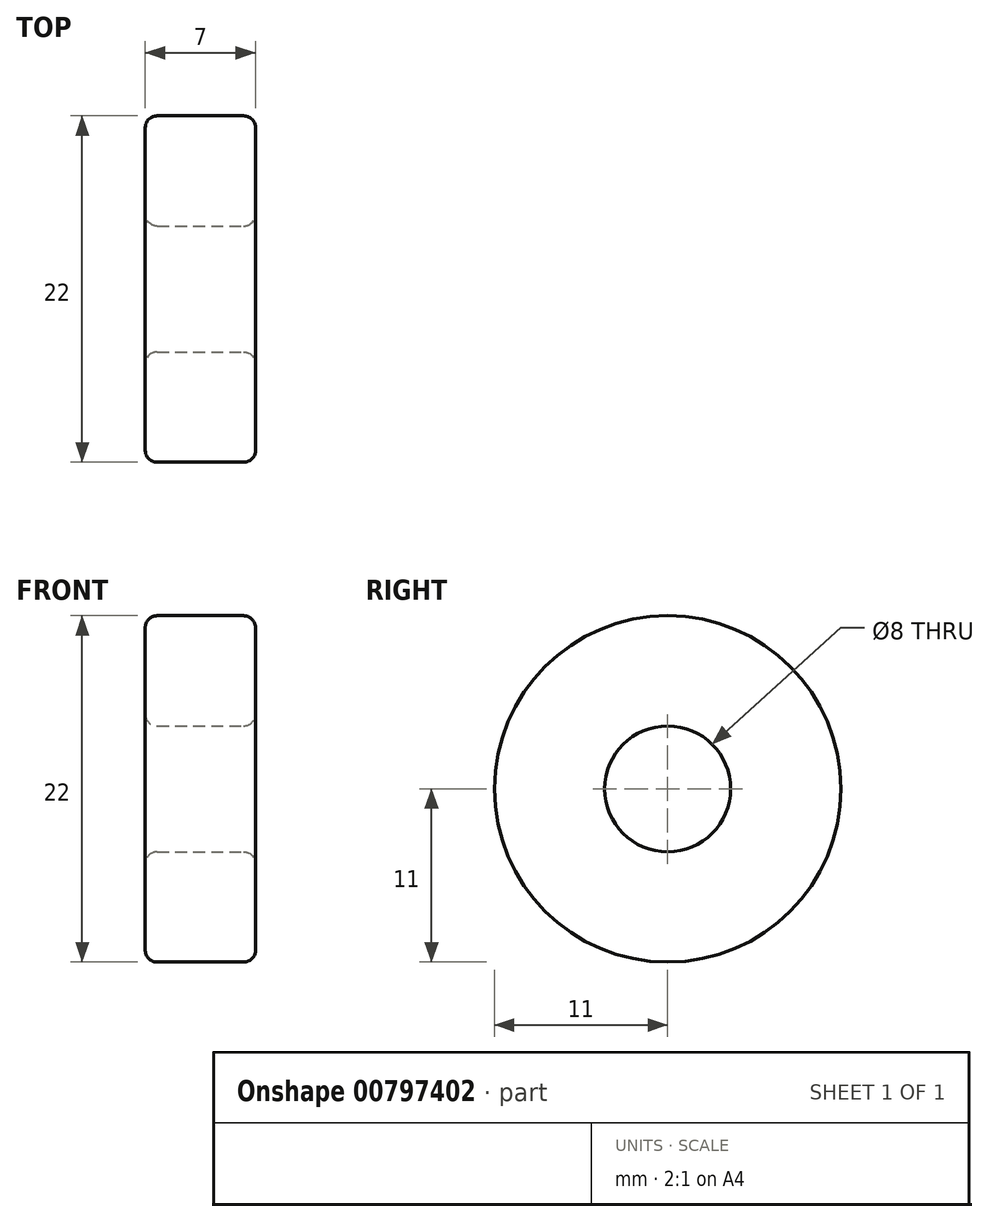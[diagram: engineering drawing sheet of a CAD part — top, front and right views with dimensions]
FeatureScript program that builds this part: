
annotation { "Feature Type Name" : "Feature", "Feature Type Description" : "" }
export const myFeature = defineFeature(function(context is Context, id is Id, definition is map)
    precondition{}
    {
        {
            var Q0;
            Q0=qCreatedBy(makeId("Front.planeOp"),FACE);
            var sketch = newSketch(context, id + "F0", { "sketchPlane" : qUnion([Q0])});
            skLineSegment(sketch, "E0.bottom", {"start": v(-3.5, 11) * mm, "end": v(3.5, 11) * mm});
            skLineSegment(sketch, "E0.top", {"start": v(-3.5, 4) * mm, "end": v(3.5, 4) * mm});
            skLineSegment(sketch, "E0.left", {"start": v(-3.5, 11) * mm, "end": v(-3.5, 4) * mm});
            skLineSegment(sketch, "E0.right", {"start": v(3.5, 11) * mm, "end": v(3.5, 4) * mm});
            skPoint(sketch, "E1", {"position": v(0, 11) * mm});
            skLineSegment(sketch, "E2", {"start": v(5.31, 0) * mm, "end": v(-6.65, 0) * mm, "construction": true});
            skSolve(sketch);
        }
        {
            var Q0;
            Q0=qSketchRegion(id+"F0",true);
            var Q1;
            Q1=sQuery(id+"F0.wireOp",EDGE,"E2");
            revolve(context, id + "F1", {"entities" : qUnion([Q0]), "axis" : qUnion([Q1]), "revolveType" : RevolveType.FULL});
        }
        {
            var Q0;
            Q0=makeQuery(id+"F1.opRevolve","SWEPT_EDGE",EDGE,{"disambiguationData":[OSD([sQuery(id+"F0.wireOp",EDGE,"E0.bottom"),sQuery(id+"F0.wireOp",EDGE,"E0.left")])]});
            var Q1;
            Q1=makeQuery(id+"F1.opRevolve","SWEPT_EDGE",EDGE,{"disambiguationData":[OSD([sQuery(id+"F0.wireOp",EDGE,"E0.top"),sQuery(id+"F0.wireOp",EDGE,"E0.left")])]});
            var Q2;
            Q2=makeQuery(id+"F1.opRevolve","SWEPT_EDGE",EDGE,{"disambiguationData":[OSD([sQuery(id+"F0.wireOp",EDGE,"E0.bottom"),sQuery(id+"F0.wireOp",EDGE,"E0.right")])]});
            var Q3;
            Q3=makeQuery(id+"F1.opRevolve","SWEPT_EDGE",EDGE,{"disambiguationData":[OSD([sQuery(id+"F0.wireOp",EDGE,"E0.top"),sQuery(id+"F0.wireOp",EDGE,"E0.right")])]});
            fillet(context, id + "F2", {"entities" : qUnion([Q0, Q1, Q2, Q3]), "radius" : 0.75 * mm, "tangentPropagation" : true, "allowEdgeOverflow" : false});
        }
    });
